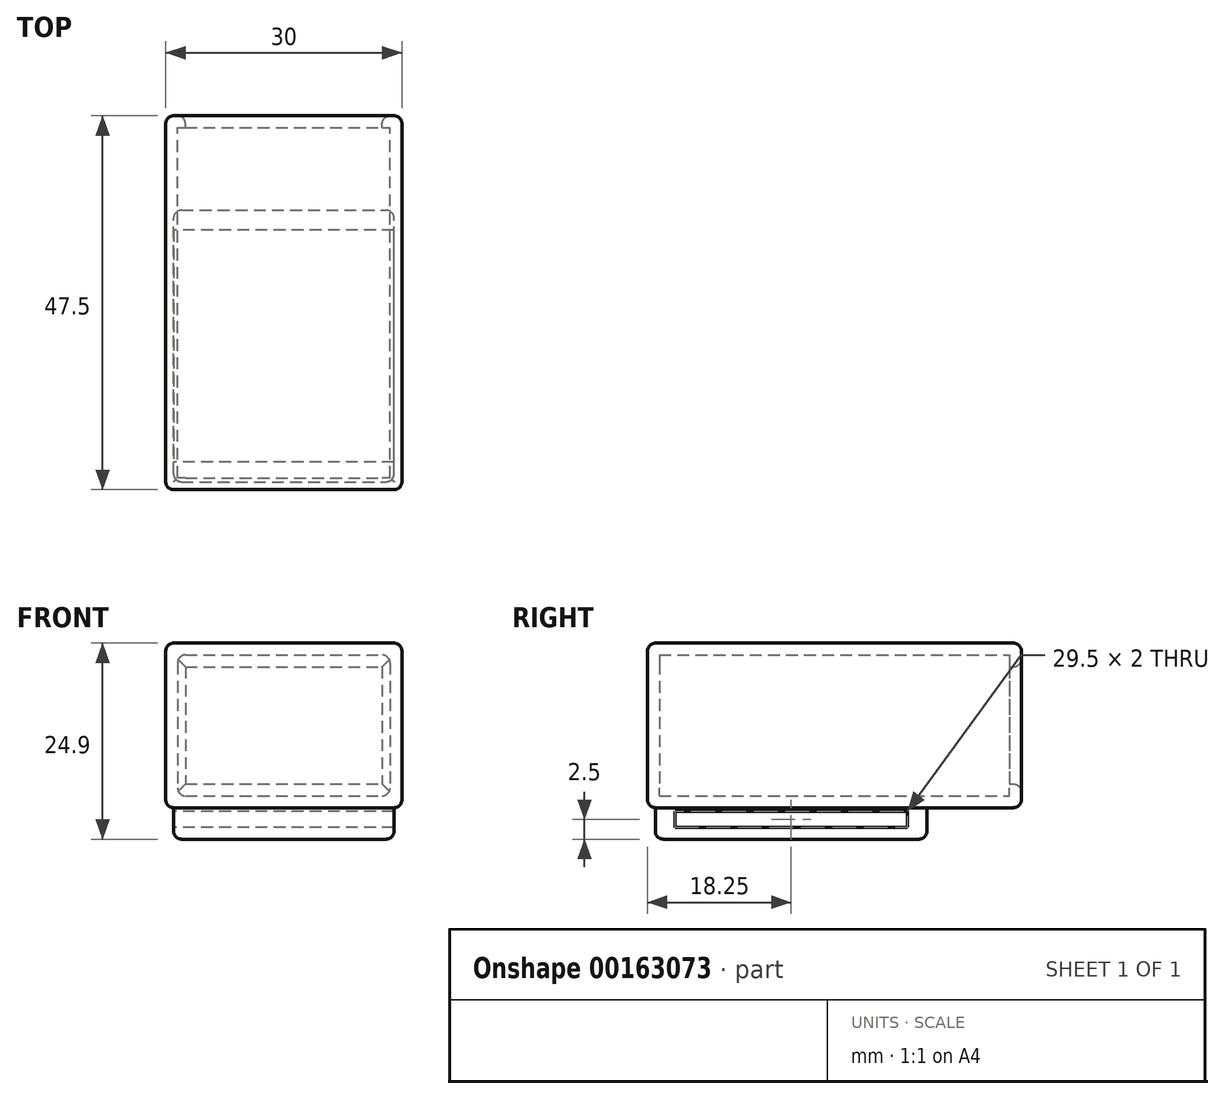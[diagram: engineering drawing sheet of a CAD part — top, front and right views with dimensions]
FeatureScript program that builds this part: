
annotation { "Feature Type Name" : "Feature", "Feature Type Description" : "" }
export const myFeature = defineFeature(function(context is Context, id is Id, definition is map)
    precondition{}
    {
        {
            var Q0;
            Q0=qCreatedBy(makeId("Front.planeOp"),FACE);
            var sketch = newSketch(context, id + "F0", { "sketchPlane" : qUnion([Q0])});
            skLineSegment(sketch, "E0.bottom", {"start": v(-13.5, 8.95) * mm, "end": v(13.5, 8.95) * mm});
            skLineSegment(sketch, "E0.top", {"start": v(-13.5, -8.95) * mm, "end": v(13.5, -8.95) * mm});
            skLineSegment(sketch, "E0.left", {"start": v(-13.5, 8.95) * mm, "end": v(-13.5, -8.95) * mm});
            skLineSegment(sketch, "E0.right", {"start": v(13.5, 8.95) * mm, "end": v(13.5, -8.95) * mm});
            skPoint(sketch, "E0.middle", {"position": v(0, 0) * mm});
            skLineSegment(sketch, "E1.bottom", {"start": v(-15, 10.45) * mm, "end": v(15, 10.45) * mm});
            skLineSegment(sketch, "E1.top", {"start": v(-15, -10.45) * mm, "end": v(15, -10.45) * mm});
            skLineSegment(sketch, "E1.left", {"start": v(-15, 10.45) * mm, "end": v(-15, -10.45) * mm});
            skLineSegment(sketch, "E1.right", {"start": v(15, 10.45) * mm, "end": v(15, -10.45) * mm});
            skSolve(sketch);
        }
        {
            var Q0;
            Q0 = qSketchRegion(id + "F0", true);
            extrude(context, id + "F1", {"entities" : qUnion([Q0]), "depth" : 34 * mm});
        }
        {
            var Q0;
            Q0=makeQuery(id+"F1.opExtrude","CAP_FACE",FACE,{"disambiguationData":[OSD([sQuery(id+"F0.wireOp",EDGE,"E0.bottom"),sQuery(id+"F0.wireOp",EDGE,"E0.top"),sQuery(id+"F0.wireOp",EDGE,"E0.left"),sQuery(id+"F0.wireOp",EDGE,"E0.right"),sQuery(id+"F0.wireOp",EDGE,"E1.bottom"),sQuery(id+"F0.wireOp",EDGE,"E1.top"),sQuery(id+"F0.wireOp",EDGE,"E1.left"),sQuery(id+"F0.wireOp",EDGE,"E1.right")])],"isStart":false});
            var sketch = newSketch(context, id + "F2", { "sketchPlane" : qUnion([Q0])});
            skLineSegment(sketch, "E2.bottom", {"start": v(15, 10.45) * mm, "end": v(-15, 10.45) * mm});
            skLineSegment(sketch, "E2.top", {"start": v(15, -10.45) * mm, "end": v(-15, -10.45) * mm});
            skLineSegment(sketch, "E2.left", {"start": v(15, 10.45) * mm, "end": v(15, -10.45) * mm});
            skLineSegment(sketch, "E2.right", {"start": v(-15, 10.45) * mm, "end": v(-15, -10.45) * mm});
            skPoint(sketch, "E2.middle", {"position": v(0, 0) * mm});
            skSolve(sketch);
        }
        {
            var Q0;
            Q0 = qSketchRegion(id + "F2", true);
            extrude(context, id + "F3", {"entities" : qUnion([Q0]), "operationType" : NewBodyOperationType.ADD, "depth" : 1.5 * mm});
        }
        {
            var Q0;
            Q0=qCreatedBy(makeId("Front.planeOp"),FACE);
            var sketch = newSketch(context, id + "F4", { "sketchPlane" : qUnion([Q0])});
            skLineSegment(sketch, "E3.bottom", {"start": v(-15, 10.45) * mm, "end": v(15, 10.45) * mm});
            skLineSegment(sketch, "E3.top", {"start": v(-15, -10.45) * mm, "end": v(15, -10.45) * mm});
            skLineSegment(sketch, "E3.left", {"start": v(-15, 10.45) * mm, "end": v(-15, -10.45) * mm});
            skLineSegment(sketch, "E3.right", {"start": v(15, 10.45) * mm, "end": v(15, -10.45) * mm});
            skPoint(sketch, "E3.middle", {"position": v(0, 0) * mm});
            skLineSegment(sketch, "E4.bottom", {"start": v(-13.5, 8.95) * mm, "end": v(13.5, 8.95) * mm});
            skLineSegment(sketch, "E4.top", {"start": v(-13.5, -8.95) * mm, "end": v(13.5, -8.95) * mm});
            skLineSegment(sketch, "E4.left", {"start": v(-13.5, 8.95) * mm, "end": v(-13.5, -8.95) * mm});
            skLineSegment(sketch, "E4.right", {"start": v(13.5, 8.95) * mm, "end": v(13.5, -8.95) * mm});
            skSolve(sketch);
        }
        {
            var Q0;
            Q0 = qSketchRegion(id + "F4", true);
            extrude(context, id + "F5", {"entities" : qUnion([Q0]), "oppositeDirection" : true, "depth" : 12 * mm});
        }
        {
            var Q0;
            Q0=makeQuery(id+"F5.opExtrude","CAP_FACE",FACE,{"disambiguationData":[OSD([sQuery(id+"F4.wireOp",EDGE,"E3.bottom"),sQuery(id+"F4.wireOp",EDGE,"E3.top"),sQuery(id+"F4.wireOp",EDGE,"E3.left"),sQuery(id+"F4.wireOp",EDGE,"E3.right"),sQuery(id+"F4.wireOp",EDGE,"E4.bottom"),sQuery(id+"F4.wireOp",EDGE,"E4.top"),sQuery(id+"F4.wireOp",EDGE,"E4.left"),sQuery(id+"F4.wireOp",EDGE,"E4.right")])],"isStart":false});
            var sketch = newSketch(context, id + "F6", { "sketchPlane" : qUnion([Q0])});
            skLineSegment(sketch, "E5.bottom", {"start": v(13.5, 8.95) * mm, "end": v(-13.5, 8.95) * mm});
            skLineSegment(sketch, "E5.top", {"start": v(13.5, -8.95) * mm, "end": v(-13.5, -8.95) * mm});
            skLineSegment(sketch, "E5.left", {"start": v(13.5, 8.95) * mm, "end": v(13.5, -8.95) * mm});
            skLineSegment(sketch, "E5.right", {"start": v(-13.5, 8.95) * mm, "end": v(-13.5, -8.95) * mm});
            skPoint(sketch, "E5.middle", {"position": v(0, 0) * mm});
            skLineSegment(sketch, "E6.bottom", {"start": v(12.5, 7.45) * mm, "end": v(-12.5, 7.45) * mm});
            skLineSegment(sketch, "E6.top", {"start": v(12.5, -7.45) * mm, "end": v(-12.5, -7.45) * mm});
            skLineSegment(sketch, "E6.left", {"start": v(12.5, 7.45) * mm, "end": v(12.5, -7.45) * mm});
            skLineSegment(sketch, "E6.right", {"start": v(-12.5, 7.45) * mm, "end": v(-12.5, -7.45) * mm});
            skSolve(sketch);
        }
        {
            var Q0;
            Q0 = qSketchRegion(id + "F6", true);
            extrude(context, id + "F7", {"entities" : qUnion([Q0]), "operationType" : NewBodyOperationType.ADD, "oppositeDirection" : true, "depth" : 1.5 * mm});
        }
        {
            var Q0;
            Q0=makeQuery(id+"F3.boolean.opBoolean","MERGE",EDGE,{"derivedFrom":[makeQuery(id+"F1.opExtrude","SWEPT_EDGE",EDGE,{"disambiguationData":[OSD([sQuery(id+"F0.wireOp",EDGE,"E1.bottom"),sQuery(id+"F0.wireOp",EDGE,"E1.right")])]}),makeQuery(id+"F3.opExtrude","SWEPT_EDGE",EDGE,{"disambiguationData":[OSD([sQuery(id+"F2.wireOp",EDGE,"E2.bottom"),sQuery(id+"F2.wireOp",EDGE,"E2.left")])]})]});
            var Q1;
            Q1=makeQuery(id+"F5.opExtrude","SWEPT_EDGE",EDGE,{"disambiguationData":[OSD([sQuery(id+"F4.wireOp",EDGE,"E3.bottom"),sQuery(id+"F4.wireOp",EDGE,"E3.right")])]});
            var Q2;
            Q2=makeQuery(id+"F5.opExtrude","SWEPT_EDGE",EDGE,{"disambiguationData":[OSD([sQuery(id+"F4.wireOp",EDGE,"E3.top"),sQuery(id+"F4.wireOp",EDGE,"E3.right")])]});
            var Q3;
            Q3=makeQuery(id+"F3.boolean.opBoolean","MERGE",EDGE,{"derivedFrom":[makeQuery(id+"F1.opExtrude","SWEPT_EDGE",EDGE,{"disambiguationData":[OSD([sQuery(id+"F0.wireOp",EDGE,"E1.top"),sQuery(id+"F0.wireOp",EDGE,"E1.right")])]}),makeQuery(id+"F3.opExtrude","SWEPT_EDGE",EDGE,{"disambiguationData":[OSD([sQuery(id+"F2.wireOp",EDGE,"E2.top"),sQuery(id+"F2.wireOp",EDGE,"E2.left")])]})]});
            var Q4;
            Q4=makeQuery(id+"F5.opExtrude","SWEPT_EDGE",EDGE,{"disambiguationData":[OSD([sQuery(id+"F4.wireOp",EDGE,"E3.bottom"),sQuery(id+"F4.wireOp",EDGE,"E3.left")])]});
            var Q5;
            Q5=makeQuery(id+"F3.boolean.opBoolean","MERGE",EDGE,{"derivedFrom":[makeQuery(id+"F1.opExtrude","SWEPT_EDGE",EDGE,{"disambiguationData":[OSD([sQuery(id+"F0.wireOp",EDGE,"E1.bottom"),sQuery(id+"F0.wireOp",EDGE,"E1.left")])]}),makeQuery(id+"F3.opExtrude","SWEPT_EDGE",EDGE,{"disambiguationData":[OSD([sQuery(id+"F2.wireOp",EDGE,"E2.bottom"),sQuery(id+"F2.wireOp",EDGE,"E2.right")])]})]});
            var Q6;
            Q6=makeQuery(id+"F5.opExtrude","CAP_EDGE",EDGE,{"disambiguationData":[OSD([sQuery(id+"F4.wireOp",EDGE,"E3.bottom")])],"isStart":false});
            var Q7;
            Q7=makeQuery(id+"F5.opExtrude","CAP_EDGE",EDGE,{"disambiguationData":[OSD([sQuery(id+"F4.wireOp",EDGE,"E3.right")])],"isStart":false});
            var Q8;
            Q8=makeQuery(id+"F5.opExtrude","CAP_EDGE",EDGE,{"disambiguationData":[OSD([sQuery(id+"F4.wireOp",EDGE,"E3.left")])],"isStart":false});
            var Q9;
            Q9=makeQuery(id+"F5.opExtrude","CAP_EDGE",EDGE,{"disambiguationData":[OSD([sQuery(id+"F4.wireOp",EDGE,"E3.top")])],"isStart":false});
            var Q10;
            Q10=makeQuery(id+"F7.opExtrude","CAP_EDGE",EDGE,{"disambiguationData":[OSD([sQuery(id+"F6.wireOp",EDGE,"E6.top")])],"isStart":true});
            var Q11;
            Q11=makeQuery(id+"F7.opExtrude","CAP_EDGE",EDGE,{"disambiguationData":[OSD([sQuery(id+"F6.wireOp",EDGE,"E6.left")])],"isStart":true});
            var Q12;
            Q12=makeQuery(id+"F7.opExtrude","CAP_EDGE",EDGE,{"disambiguationData":[OSD([sQuery(id+"F6.wireOp",EDGE,"E6.right")])],"isStart":true});
            var Q13;
            Q13=makeQuery(id+"F7.opExtrude","CAP_EDGE",EDGE,{"disambiguationData":[OSD([sQuery(id+"F6.wireOp",EDGE,"E6.bottom")])],"isStart":true});
            var Q14;
            Q14=makeQuery(id+"F3.opExtrude","CAP_EDGE",EDGE,{"disambiguationData":[OSD([sQuery(id+"F2.wireOp",EDGE,"E2.bottom")])],"isStart":false});
            var Q15;
            Q15=makeQuery(id+"F3.opExtrude","CAP_EDGE",EDGE,{"disambiguationData":[OSD([sQuery(id+"F2.wireOp",EDGE,"E2.left")])],"isStart":false});
            var Q16;
            Q16=makeQuery(id+"F3.opExtrude","CAP_EDGE",EDGE,{"disambiguationData":[OSD([sQuery(id+"F2.wireOp",EDGE,"E2.top")])],"isStart":false});
            var Q17;
            Q17=makeQuery(id+"F3.opExtrude","CAP_EDGE",EDGE,{"disambiguationData":[OSD([sQuery(id+"F2.wireOp",EDGE,"E2.right")])],"isStart":false});
            var Q18;
            Q18=makeQuery(id+"F3.boolean.opBoolean","MERGE",EDGE,{"derivedFrom":[makeQuery(id+"F1.opExtrude","SWEPT_EDGE",EDGE,{"disambiguationData":[OSD([sQuery(id+"F0.wireOp",EDGE,"E1.top"),sQuery(id+"F0.wireOp",EDGE,"E1.left")])]}),makeQuery(id+"F3.opExtrude","SWEPT_EDGE",EDGE,{"disambiguationData":[OSD([sQuery(id+"F2.wireOp",EDGE,"E2.top"),sQuery(id+"F2.wireOp",EDGE,"E2.right")])]})]});
            var Q19;
            Q19=makeQuery(id+"F5.opExtrude","SWEPT_EDGE",EDGE,{"disambiguationData":[OSD([sQuery(id+"F4.wireOp",EDGE,"E3.top"),sQuery(id+"F4.wireOp",EDGE,"E3.left")])]});
            var Q20;
            Q20=makeQuery(id+"F1.opExtrude","SWEPT_EDGE",EDGE,{"disambiguationData":[OSD([sQuery(id+"F0.wireOp",EDGE,"E0.top"),sQuery(id+"F0.wireOp",EDGE,"E0.left")])]});
            var Q21;
            Q21=makeQuery(id+"F1.opExtrude","SWEPT_EDGE",EDGE,{"disambiguationData":[OSD([sQuery(id+"F0.wireOp",EDGE,"E0.top"),sQuery(id+"F0.wireOp",EDGE,"E0.right")])]});
            var Q22;
            Q22=makeQuery(id+"F1.opExtrude","SWEPT_EDGE",EDGE,{"disambiguationData":[OSD([sQuery(id+"F0.wireOp",EDGE,"E0.bottom"),sQuery(id+"F0.wireOp",EDGE,"E0.right")])]});
            var Q23;
            Q23=makeQuery(id+"F1.opExtrude","SWEPT_EDGE",EDGE,{"disambiguationData":[OSD([sQuery(id+"F0.wireOp",EDGE,"E0.bottom"),sQuery(id+"F0.wireOp",EDGE,"E0.left")])]});
            var Q24;
            Q24=makeQuery(id+"F5.opExtrude","SWEPT_EDGE",EDGE,{"disambiguationData":[OSD([sQuery(id+"F4.wireOp",EDGE,"E4.top"),sQuery(id+"F4.wireOp",EDGE,"E4.left")])]});
            var Q25;
            Q25=makeQuery(id+"F5.opExtrude","SWEPT_EDGE",EDGE,{"disambiguationData":[OSD([sQuery(id+"F4.wireOp",EDGE,"E4.bottom"),sQuery(id+"F4.wireOp",EDGE,"E4.left")])]});
            var Q26;
            Q26=makeQuery(id+"F5.opExtrude","SWEPT_EDGE",EDGE,{"disambiguationData":[OSD([sQuery(id+"F4.wireOp",EDGE,"E4.top"),sQuery(id+"F4.wireOp",EDGE,"E4.right")])]});
            var Q27;
            Q27=makeQuery(id+"F5.opExtrude","SWEPT_EDGE",EDGE,{"disambiguationData":[OSD([sQuery(id+"F4.wireOp",EDGE,"E4.bottom"),sQuery(id+"F4.wireOp",EDGE,"E4.right")])]});
            fillet(context, id + "F8", {"entities" : qUnion([Q0, Q1, Q2, Q3, Q4, Q5, Q6, Q7, Q8, Q9, Q10, Q11, Q12, Q13, Q14, Q15, Q16, Q17, Q18, Q19, Q20, Q21, Q22, Q23, Q24, Q25, Q26, Q27]), "radius" : 1 * mm, "tangentPropagation" : true, "allowEdgeOverflow" : false});
        }
        {
            var Q0;
            Q0=makeQuery(id+"F3.boolean.opBoolean","MERGE",FACE,{"derivedFrom":[makeQuery(id+"F1.opExtrude","SWEPT_FACE",FACE,{"disambiguationData":[OSD([sQuery(id+"F0.wireOp",EDGE,"E1.top")])]}),makeQuery(id+"F3.opExtrude","SWEPT_FACE",FACE,{"disambiguationData":[OSD([sQuery(id+"F2.wireOp",EDGE,"E2.top")])]})]});
            var sketch = newSketch(context, id + "F9", { "sketchPlane" : qUnion([Q0])});
            skLineSegment(sketch, "E7.bottom", {"start": v(14, 34.5) * mm, "end": v(-14, 34.5) * mm});
            skLineSegment(sketch, "E7.top", {"start": v(14, 0) * mm, "end": v(-14, 0) * mm});
            skLineSegment(sketch, "E7.left", {"start": v(14, 34.5) * mm, "end": v(14, 0) * mm});
            skLineSegment(sketch, "E7.right", {"start": v(-14, 34.5) * mm, "end": v(-14, 0) * mm});
            skSolve(sketch);
        }
        {
            var Q0;
            Q0 = qSketchRegion(id + "F9", true);
            extrude(context, id + "F10", {"entities" : qUnion([Q0]), "operationType" : NewBodyOperationType.ADD, "depth" : 4 * mm});
        }
        {
            var Q0;
            Q0=makeQuery(id+"F10.opExtrude","SWEPT_FACE",FACE,{"disambiguationData":[OSD([sQuery(id+"F9.wireOp",EDGE,"E7.right")])]});
            var sketch = newSketch(context, id + "F11", { "sketchPlane" : qUnion([Q0])});
            skLineSegment(sketch, "E8.bottom", {"start": v(2.5, -10.95) * mm, "end": v(32, -10.95) * mm});
            skLineSegment(sketch, "E8.top", {"start": v(2.5, -12.95) * mm, "end": v(32, -12.95) * mm});
            skLineSegment(sketch, "E8.left", {"start": v(2.5, -10.95) * mm, "end": v(2.5, -12.95) * mm});
            skLineSegment(sketch, "E8.right", {"start": v(32, -10.95) * mm, "end": v(32, -12.95) * mm});
            skSolve(sketch);
        }
        {
            var Q0;
            Q0 = qSketchRegion(id + "F11", true);
            var Q1;
            Q1=makeQuery(id+"F10.opExtrude","SWEPT_FACE",FACE,{"disambiguationData":[OSD([sQuery(id+"F9.wireOp",EDGE,"E7.left")])]});
            extrude(context, id + "F12", {"entities" : qUnion([Q0]), "operationType" : NewBodyOperationType.REMOVE, "endBound" : BoundingType.UP_TO_SURFACE, "oppositeDirection" : true, "endBoundEntityFace" : qUnion([Q1]), "depth" : 25 * mm});
        }
        {
            var Q0;
            Q0=makeQuery(id+"F10.opExtrude","CAP_FACE",FACE,{"disambiguationData":[OSD([sQuery(id+"F9.wireOp",EDGE,"E7.bottom"),sQuery(id+"F9.wireOp",EDGE,"E7.top"),sQuery(id+"F9.wireOp",EDGE,"E7.left"),sQuery(id+"F9.wireOp",EDGE,"E7.right")])],"isStart":false});
            var Q1;
            Q1=makeQuery(id+"F10.opExtrude","SWEPT_EDGE",EDGE,{"disambiguationData":[OSD([sQuery(id+"F9.wireOp",EDGE,"E7.top"),sQuery(id+"F9.wireOp",EDGE,"E7.left")])]});
            var Q2;
            Q2=makeQuery(id+"F10.opExtrude","SWEPT_EDGE",EDGE,{"disambiguationData":[OSD([sQuery(id+"F9.wireOp",EDGE,"E7.bottom"),sQuery(id+"F9.wireOp",EDGE,"E7.left")])]});
            var Q3;
            Q3=makeQuery(id+"F12.boolean.opBoolean","COPY",EDGE,{"derivedFrom":makeQuery(id+"F12.opExtrude","CAP_EDGE",EDGE,{"disambiguationData":[OSD([sQuery(id+"F11.wireOp",EDGE,"E8.bottom")])],"isStart":false})});
            var Q4;
            Q4=makeQuery(id+"F12.boolean.opBoolean","COPY",EDGE,{"derivedFrom":makeQuery(id+"F12.opExtrude","CAP_EDGE",EDGE,{"disambiguationData":[OSD([sQuery(id+"F11.wireOp",EDGE,"E8.right")])],"isStart":false})});
            var Q5;
            Q5=makeQuery(id+"F12.boolean.opBoolean","COPY",EDGE,{"derivedFrom":makeQuery(id+"F12.opExtrude","CAP_EDGE",EDGE,{"disambiguationData":[OSD([sQuery(id+"F11.wireOp",EDGE,"E8.left")])],"isStart":false})});
            var Q6;
            Q6=makeQuery(id+"F10.opExtrude","SWEPT_EDGE",EDGE,{"disambiguationData":[OSD([sQuery(id+"F9.wireOp",EDGE,"E7.top"),sQuery(id+"F9.wireOp",EDGE,"E7.right")])]});
            var Q7;
            Q7=makeQuery(id+"F12.boolean.opBoolean","COPY",EDGE,{"derivedFrom":makeQuery(id+"F12.opExtrude","CAP_EDGE",EDGE,{"disambiguationData":[OSD([sQuery(id+"F11.wireOp",EDGE,"E8.left")])],"isStart":true})});
            var Q8;
            Q8=makeQuery(id+"F12.boolean.opBoolean","COPY",EDGE,{"derivedFrom":makeQuery(id+"F12.opExtrude","CAP_EDGE",EDGE,{"disambiguationData":[OSD([sQuery(id+"F11.wireOp",EDGE,"E8.bottom")])],"isStart":true})});
            var Q9;
            Q9=makeQuery(id+"F12.boolean.opBoolean","COPY",EDGE,{"derivedFrom":makeQuery(id+"F12.opExtrude","CAP_EDGE",EDGE,{"disambiguationData":[OSD([sQuery(id+"F11.wireOp",EDGE,"E8.right")])],"isStart":true})});
            var Q10;
            Q10=makeQuery(id+"F10.opExtrude","SWEPT_EDGE",EDGE,{"disambiguationData":[OSD([sQuery(id+"F9.wireOp",EDGE,"E7.bottom"),sQuery(id+"F9.wireOp",EDGE,"E7.right")])]});
            fillet(context, id + "F13", {"entities" : qUnion([Q0, Q1, Q2, Q3, Q4, Q5, Q6, Q7, Q8, Q9, Q10]), "radius" : 1 * mm, "tangentPropagation" : true, "allowEdgeOverflow" : false});
        }
    });
